# Revit family: Pump_Commercial-Sewage_Dewatering-Zoeller-600_Horizontal_Series
name_source: partatom
category: Mechanical Equipment
units: mm (PartAtom-declared; Revit-internal decimal feet)

## family parameters
Always vertical = No
Cut with Voids When Loaded = No
OmniClass Number = 23.60.30.21
OmniClass Title = Pumps
Part Type = Normal
Room Calculation Point = No
Round Connector Dimension = Use Radius
Shared = Yes
Work Plane-Based = Yes

## types (46) — shared parameters
Assembly Code = D2010900
Connecter Description = 3" NPT (optional 3" or 4" flange available)
Cooling = Oil filled
Cord Type = UL listed 3-wire cord.
Default Elevation = 0"
Description = Horizontal Discharge. Submersible Sewage Or Dewatering Non-Clog Pump for Hazardous Environment
Gasket = Buna-N square ring seals
Hardware = Stainless Steel
Height = 29 1/4"
Hertz = 60
Impeller Type (Default) = Ductile Iron Semi-Open
Installation Type = Floor Mounted
Insulation = Class F
Lead Wires Insulation = Class F
Length = 12 5/8"
Lower Bearing = Ball bearing
Manufacturer = Zoeller
Material = Cast Iron-Zoeller-Powder Coated Epoxy
Max. Water Temp. = 104 °F
Mechanical Seals = Tandem carbon and ceramic
Min. Recommended Fluid Level = 24"
Motor Design Letter = NEMA B
Motor Protection = Thermal sensors with automatic reset.
Motor Shaft = Stainless Steel
Operation = Non-Automatic
Price = Prices may vary. Please consult Manufacturer Representative for most up-to-date price list.
RPM = 1750
Revised Date = 04/23/2024
Solid Handling = 2 1/2 Spherical Solids
Tandem Seals = Standard
Type SOW Power Cord Length = 300"
URL = http://www.zoellerpumps.com
Upper Bearing = Ball bearing
Warranty Information = 18 Months (Limited)
Waste Connection = Yes

## per-type parameters (varying)
| type | Amps | Apparent Load | Discharge Diameter | Discharge Radius | Flange Radius | Flow 611-651 @ 5', 661 @ 10' | Maximum Head | Model | Motor | Phase | Product Documentation Link | Product Page URL | Type | Void Visibility | Void Visibility 2 | Voltage | Width |
| E611 - 3" 230V/1Ph/6.9A/1HP | 7 A | 1587 VA | 3" | 1 1/2" | 3 3/4" | 250 GPM | 264" | E611-3" | 1.0 HP | 1 | http://cdn.qleapahead.com | http://www.zoellerpumps.com | Capacitor Start/Capacitor Run | 0" | 9 7/8" | 230 V | 15 15/16" |
| J611 - 3" 200V/3Ph/4.8A/1HP | 5 A | 960 VA | 3" | 1 1/2" | 3 3/4" | 250 GPM | 264" | J611-3" | 1.0 HP | 3 | http://cdn.qleapahead.com | http://www.zoellerpumps.com | 3 Phase | 0" | 9 7/8" | 200 V | 15 15/16" |
| F611 - 3" 230V/3Ph/4.2A/1HP | 4 A | 966 VA | 3" | 1 1/2" | 3 3/4" | 250 GPM | 264" | X611-3" | 1.0 HP | 3 |  | http://www.zoellerpumps.com | 3 Phase | 0" | 9 7/8" | 230 V | 15 15/16" |
| G611 - 3" 460V/3Ph/2.1A/1HP | 2 A | 966 VA | 3" | 1 1/2" | 3 3/4" | 250 GPM | 264" | G611-3" | 1.0 HP | 3 | http://cdn.qleapahead.com | http://www.zoellerpumps.com | 3 Phase | 0" | 9 7/8" | 460 V | 15 15/16" |
| E611 - 4" 230V/1Ph/6.9A/1HP | 7 A | 1587 VA | 4" | 2" | 4 1/2" | 250 GPM | 264" | E611-4" | 1.0 HP | 1 | http://cdn.qleapahead.com | http://www.zoellerpumps.com | Capacitor Star/Capacitor Run | 9 7/8" | 0" | 230 V | 17 5/16" |
| J611 - 4" 200V/3Ph/4.8A/1HP | 5 A | 960 VA | 4" | 2" | 4 1/2" | 250 GPM | 264" | J611-4" | 1.0 HP | 3 | http://cdn.qleapahead.com | http://www.zoellerpumps.com | 3 Phase | 9 7/8" | 0" | 200 V | 17 5/16" |
| F611 - 4" 230V/3Ph/4.2A/1HP | 4 A | 966 VA | 4" | 2" | 4 1/2" | 250 GPM | 264" | F611-4" | 1.0 HP | 3 | http://cdn.qleapahead.com | http://www.zoellerpumps.com | 3 Phase | 9 7/8" | 0" | 230 V | 17 5/16" |
| G611 - 4" 460V/3Ph/2.1A/1HP | 2 A | 966 VA | 4" | 2" | 4 1/2" | 250 GPM | 264" | G611-4" | 1.0 HP | 3 | http://cdn.qleapahead.com | http://www.zoellerpumps.com | 3 Phase | 9 7/8" | 0" | 460 V | 17 5/16" |
| E621 - 3" 230V/1Ph/8.9A/1.5HP | 9 A | 2047 VA | 3" | 1 1/2" | 3 3/4" | 321 GPM | 348" | E621-3" | 1.5 HP | 1 | http://cdn.qleapahead.com | http://www.zoellerpumps.com | Capacitor Star/Capacitor Run | 0" | 9 7/8" | 230 V | 15 15/16" |
| J621 - 3" 200V/3Ph/5.9A/1.5HP | 6 A | 1180 VA | 3" | 1 1/2" | 3 3/4" | 320 GPM | 348" | J621-3" | 1.5 HP | 3 | http://cdn.qleapahead.com | http://www.zoellerpumps.com | 3 Phase | 0" | 9 7/8" | 200 V | 15 15/16" |
| F621 - 3" 230V/3Ph/5.1A/1.5HP | 5 A | 1173 VA | 3" | 1 1/2" | 3 3/4" | 320 GPM | 348" | F621-3" | 1.5 HP | 3 | http://cdn.qleapahead.com | http://www.zoellerpumps.com | 3 Phase | 0" | 9 7/8" | 230 V | 15 15/16" |
| G621 - 3" 460V/3Ph/2.6A/1.5HP | 3 A | 1196 VA | 3" | 1 1/2" | 3 3/4" | 320 GPM | 348" | G621-3" | 1.5 HP | 3 | http://cdn.qleapahead.com | http://www.zoellerpumps.com | 3 Phase | 0" | 9 7/8" | 460 V | 15 15/16" |
| E621 - 4" 230V/1Ph/8.9A/1.5HP | 9 A | 2047 VA | 4" | 2" | 4 1/2" | 320 GPM | 348" | E621-4" | 1.5 HP | 1 | http://cdn.qleapahead.com | http://www.zoellerpumps.com | Capacitor Star/Capacitor Run | 9 7/8" | 0" | 230 V | 17 5/16" |
| J621 - 4" 200V/3Ph/5.9A/1.5HP | 6 A | 1180 VA | 4" | 2" | 4 1/2" | 320 GPM | 348" | J621-4" | 1.5 HP | 3 | http://cdn.qleapahead.com | http://www.zoellerpumps.com | 3 Phase | 9 7/8" | 0" | 200 V | 17 5/16" |
| F621 - 4" 230V/3Ph/5.1A/1.5HP | 5 A | 1173 VA | 4" | 2" | 4 1/2" | 320 GPM | 348" | F621-4" | 1.5 HP | 3 | http://cdn.qleapahead.com | http://www.zoellerpumps.com | 3 Phase | 9 7/8" | 0" | 230 V | 17 5/16" |
| G621 - 4" 460V/3Ph/2.6A/1.5HP | 3 A | 1196 VA | 4" | 2" | 4 1/2" | 320 GPM | 348" | G621-4" | 1.5 HP | 3 | http://cdn.qleapahead.com | http://www.zoellerpumps.com | 3 Phase | 9 7/8" | 0" | 460 V | 17 5/16" |
| E631 - 3" 230V/1Ph/14.5A/2HP | 15 A | 3335 VA | 3" | 1 1/2" | 3 3/4" | 390 GPM | 408" | E631-3" | 2.0 HP | 1 | http://cdn.qleapahead.com | http://www.zoellerpumps.com | Capacitor Star/Capacitor Run | 0" | 9 7/8" | 230 V | 15 15/16" |
| J631 - 3" 200V/3Ph/7.8A/2HP | 8 A | 1560 VA | 3" | 1 1/2" | 3 3/4" | 390 GPM | 408" | J631-3" | 2.0 HP | 3 | http://cdn.qleapahead.com | http://www.zoellerpumps.com | 3 Phase | 0" | 9 7/8" | 200 V | 15 15/16" |
| F631 - 3" 230V/3Ph/6.8A/2HP | 7 A | 1564 VA | 3" | 1 1/2" | 3 3/4" | 390 GPM | 408" | F631-3" | 2.0 HP | 3 | http://cdn.qleapahead.com | http://www.zoellerpumps.com | 3 Phase | 0" | 9 7/8" | 230 V | 15 15/16" |
| G631 - 3" 460V/3Ph/3.4A/2HP | 3 A | 1564 VA | 3" | 1 1/2" | 3 3/4" | 390 GPM | 408" | G631-3" | 2.0 HP | 3 | http://cdn.qleapahead.com | http://www.zoellerpumps.com | 3 Phase | 0" | 9 7/8" | 460 V | 15 15/16" |
| E631 - 4" 230V/1Ph/14.5A/2HP | 15 A | 3335 VA | 4" | 2" | 4 1/2" | 390 GPM | 408" | E631-4" | 2.0 HP | 1 | http://cdn.qleapahead.com | http://www.zoellerpumps.com | Capacitor Star/Capacitor Run | 9 7/8" | 0" | 230 V | 17 5/16" |
| J631 - 4" 200V/3Ph/7.8A/2HP | 8 A | 1560 VA | 4" | 2" | 4 1/2" | 390 GPM | 408" | J631-4" | 2.0 HP | 3 | http://cdn.qleapahead.com | http://www.zoellerpumps.com | 3 Phase | 9 7/8" | 0" | 200 V | 17 5/16" |
| F631 - 4" 230V/3Ph/6.8A/2HP | 7 A | 1564 VA | 4" | 2" | 4 1/2" | 390 GPM | 408" | F631-4" | 2.0 HP | 3 | http://cdn.qleapahead.com | http://www.zoellerpumps.com | 3 Phase | 9 7/8" | 0" | 230 V | 17 5/16" |
| G631 - 4" 460V/3Ph/3.4A/2HP | 3 A | 1564 VA | 4" | 2" | 4 1/2" | 390 GPM | 408" | G631-4" | 2.0 HP | 3 |  | http://www.zoellerpumps.com | 3 Phase | 9 7/8" | 0" | 460 V | 17 5/16" |
| E641 - 3" 230V/1Ph/17.0A/3HP | 17 A | 3910 VA | 3" | 1 1/2" | 3 3/4" | 420 GPM | 474" (1 Ph), 528" (3 Ph) | E641-3" | 3.0 HP | 1 | http://cdn.qleapahead.com | http://www.zoellerpumps.com | Capacitor Star/Capacitor Run | 0" | 9 7/8" | 230 V | 15 15/16" |
| J641 - 3" 200V/3Ph/11.0A/3HP | 11 A | 2200 VA | 3" | 1 1/2" | 3 3/4" | 460 GPM | 474" (1 Ph), 528" (3 Ph) | J641-3" | 3.0 HP | 3 | http://cdn.qleapahead.com | http://www.zoellerpumps.com | 3 Phase | 0" | 9 7/8" | 200 V | 15 15/16" |
| F641 - 3" 230V/3Ph/9.6A/3HP | 10 A | 2208 VA | 3" | 1 1/2" | 3 3/4" | 460 GPM | 474" (1 Ph), 528" (3 Ph) | F641-3" | 3.0 HP | 3 | http://cdn.qleapahead.com | http://www.zoellerpumps.com | 3 Phase | 0" | 9 7/8" | 230 V | 15 15/16" |
| G641 - 3" 460V/3Ph/4.8A/3HP | 5 A | 2208 VA | 3" | 1 1/2" | 3 3/4" | 460 GPM | 474" (1 Ph), 528" (3 Ph) | G641-3" | 3.0 HP | 3 | http://cdn.qleapahead.com | http://www.zoellerpumps.com | 3 Phase | 0" | 9 7/8" | 460 V | 15 15/16" |
| E641 - 4" 230V/1Ph/17.0A/3HP | 17 A | 3910 VA | 4" | 2" | 4 1/2" | 420 GPM | 474" (1 Ph), 528" (3 Ph) | E641-4" | 3.0 HP | 1 | http://cdn.qleapahead.com | http://www.zoellerpumps.com | Capacitor Star/Capacitor Run | 9 7/8" | 0" | 230 V | 17 5/16" |
| J641 - 4" 200V/3Ph/11.0A/3HP | 11 A | 2200 VA | 4" | 2" | 4 1/2" | 460 GPM | 474" (1 Ph), 528" (3 Ph) | J641-4" | 3.0 HP | 3 | http://cdn.qleapahead.com | http://www.zoellerpumps.com | 3 Phase | 9 7/8" | 0" | 200 V | 17 5/16" |
| F641 - 4" 230V/3Ph/9.6A/3HP | 10 A | 2208 VA | 4" | 2" | 4 1/2" | 460 GPM | 474" (1 Ph), 528" (3 Ph) | F641-4" | 3.0 HP | 3 | http://cdn.qleapahead.com | http://www.zoellerpumps.com | 3 Phase | 9 7/8" | 0" | 230 V | 17 5/16" |
| G641 - 4" 460V/3Ph/4.8A/3HP | 5 A | 2208 VA | 4" | 2" | 4 1/2" | 460 GPM | 474" (1 Ph), 528" (3 Ph) | G641-4" | 3.0 HP | 3 | http://cdn.qleapahead.com | http://www.zoellerpumps.com | 3 Phase | 9 7/8" | 0" | 460 V | 17 5/16" |
| E651 - 3" 230V/1Ph/28.0A/5HP | 28 A | 6440 VA | 3" | 1 1/2" | 3 3/4" | 475 GPM | 558" (1 Ph), 648" (3 Ph) | X651-3" | 5.0 HP | 1 | http://cdn.qleapahead.com | http://www.zoellerpumps.com | Capacitor Star/Capacitor Run | 0" | 9 7/8" | 230 V | 15 15/16" |
| J651 - 3" 200V/3Ph/17.5A/5HP | 18 A | 3500 VA | 3" | 1 1/2" | 3 3/4" | 533 GPM | 558" (1 Ph), 648" (3 Ph) | J651-3" | 5.0 HP | 3 | http://cdn.qleapahead.com | http://www.zoellerpumps.com | 3 Phase | 0" | 9 7/8" | 200 V | 15 15/16" |
| F651 - 3" 230V/3Ph/15.2A/5HP | 15 A | 3496 VA | 3" | 1 1/2" | 3 3/4" | 533 GPM | 558" (1 Ph), 648" (3 Ph) | F651-3" | 5.0 HP | 3 | http://cdn.qleapahead.com | http://www.zoellerpumps.com | 3 Phase | 0" | 9 7/8" | 230 V | 15 15/16" |
| G651 - 3" 460V/3Ph/7.6A/5HP | 8 A | 3496 VA | 3" | 1 1/2" | 3 3/4" | 533 GPM | 558" (1 Ph), 648" (3 Ph) | G651-3" | 5.0 HP | 3 | http://www.zoellerpumps.com | http://cdn.qleapahead.com | 3 Phase | 0" | 9 7/8" | 460 V | 15 15/16" |
| E651 - 4" 230V/1Ph/28.0A/5HP | 28 A | 6440 VA | 4" | 2" | 4 1/2" | 475 GPM | 558" (1 Ph), 648" (3 Ph) | E651-4" | 5.0 HP | 1 | http://cdn.qleapahead.com | http://www.zoellerpumps.com | Capacitor Star/Capacitor Run | 9 7/8" | 0" | 230 V | 17 5/16" |
| J651 - 4" 200V/3Ph/17.5A/5HP | 18 A | 3500 VA | 4" | 2" | 4 1/2" | 533 GPM | 558" (1 Ph), 648" (3 Ph) | J651-4" | 5.0 HP | 3 | http://cdn.qleapahead.com | http://www.zoellerpumps.com | 3 Phase | 9 7/8" | 0" | 200 V | 17 5/16" |
| F651 - 4" 230V/3Ph/15.2A/5HP | 15 A | 3496 VA | 4" | 2" | 4 1/2" | 533 GPM | 558" (1 Ph), 648" (3 Ph) | F651-4" | 5.0 HP | 3 | http://cdn.qleapahead.com | http://www.zoellerpumps.com | 3 Phase | 9 7/8" | 0" | 230 V | 17 5/16" |
| G651 - 4" 460V/3Ph/7.6A/5HP | 8 A | 3496 VA | 4" | 2" | 4 1/2" | 533 GPM | 558" (1 Ph), 648" (3 Ph) | G651-4" | 5.0 HP | 3 | http://cdn.qleapahead.com | http://www.zoellerpumps.com | 3 Phase | 9 7/8" | 0" | 460 V | 17 5/16" |
| J661 - 3" 200V/3Ph/25.3A/7.5HP | 25 A | 5060 VA | 3" | 1 1/2" | 3 3/4" | 600 GPM | 780" | J661-3" | 7.5 HP | 3 | http://cdn.qleapahead.com | http://www.zoellerpumps.com | 3 Phase | 0" | 9 7/8" | 200 V | 15 15/16" |
| F661 - 3" 230V/3Ph/22.0A/7.5HP | 22 A | 5060 VA | 3" | 1 1/2" | 3 3/4" | 600 GPM | 780" | F661-3" | 7.5 HP | 3 | http://cdn.qleapahead.com | http://www.zoellerpumps.com | 3 Phase | 0" | 9 7/8" | 230 V | 15 15/16" |
| G661 - 3" 460V/3Ph/11.0A/7.5HP | 11 A | 5060 VA | 3" | 1 1/2" | 3 3/4" | 600 GPM | 780" | G661-3" | 7.5 HP | 3 | http://cdn.qleapahead.com | http://www.zoellerpumps.com | 3 Phase | 0" | 9 7/8" | 460 V | 15 15/16" |
| J661 - 4" 200V/3Ph/25.3A/7.5HP | 25 A | 5060 VA | 4" | 2" | 4 1/2" | 600 GPM | 780" | J661-4" | 7.5 HP | 3 | http://cdn.qleapahead.com | http://www.zoellerpumps.com | 3 Phase | 9 7/8" | 0" | 200 V | 17 5/16" |
| F661 - 4" 230V/3Ph/22.0A/7.5HP | 22 A | 5060 VA | 4" | 2" | 4 1/2" | 600 GPM | 780" | F661-4" | 7.5 HP | 3 | http://cdn.qleapahead.com | http://www.zoellerpumps.com | 3 Phase | 9 7/8" | 0" | 230 V | 17 5/16" |
| G661 - 4" 460V/3Ph/11.0A/7.5HP | 11 A | 5060 VA | 4" | 2" | 4 1/2" | 600 GPM | 780" | G661-4" | 7.5 HP | 3 | http://cdn.qleapahead.com | http://www.zoellerpumps.com | 3 Phase | 9 7/8" | 0" | 460 V | 17 5/16" |

## geometry (parser evidence)
native form markers: Sweep x2
no freeform markers — native parametric forms only
